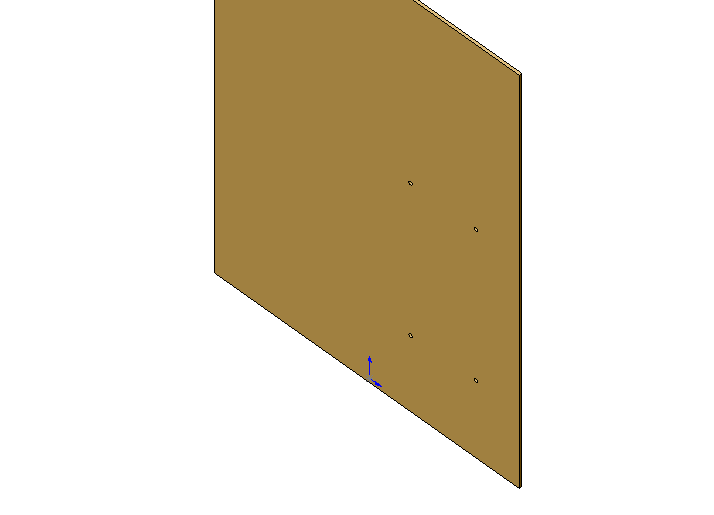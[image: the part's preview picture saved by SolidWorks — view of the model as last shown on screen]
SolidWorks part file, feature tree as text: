
SOLIDWORKS PART (.sldprt)
format: sldprt  version: not decoded by parser v0  size: 214,528 bytes
history: native  units: mm
features: thread x4, sketch x3, material x1, extrude x1, hole x1 (+12 scaffold rows collapsed)
feature tree (22):
  scaffold x12  (default folders/planes/origin — collapsed)
  material  "Material <not specified>"
  sketch  "Sketch1"  dims[D1=355.6mm D2=482.6mm]
  extrude  "Extrude1"  Depth=3.175mm
  hole  "#10 Clearance Hole1"  Diameter=4.0386mm Depth=3.175mm
  sketch  "Sketch3"
  sketch  "Sketch2"  dims[hole-wizard template sketch: 60 standard entries collapsed; hole parameters kept: c18.Thru Tap Drill Depth=3.175mm]
  thread  "Cosmetic Thread1"  Diameter=3.175mm  [1 undecoded]
  thread  "Cosmetic Thread2"  Diameter=3.175mm  [1 undecoded]
  thread  "Cosmetic Thread3"  Diameter=3.175mm  [1 undecoded]
  thread  "Cosmetic Thread4"  Diameter=3.175mm  [1 undecoded]
decode coverage: 8 of 9 modeling features carry decoded parameters
note: ~ marks probable driven/reference dimensions
note: 4 parameter values undecoded
note: suppression state not decoded; provenance and decode notes live in map.json
